FCSTD DOCUMENT  (FreeCAD 0.22R37730 (Git))
Label: Прокладка
License: All rights reserved
LicenseURL: https://en.wikipedia.org/wiki/All_rights_reserved
objects: Image::ImagePlane×1, Sketcher::SketchObject×1, PartDesign::Body×1
note: 2 computed .brp shape members not serialized (recipe doc carries the construction recipe); baked Part::Feature solids carry a one-line shape summary decoded from their .brp

FEATURE [Image::ImagePlane] Scan
  Placement = pos=(31.0997,3.57913,0) rot=(0,0,-1;1.91986rad)
  XSize = 66.6751
  YSize = 122.428
FEATURE [Sketcher::SketchObject] Sketch
  AttachmentSupport = -> [XY_Plane]
  FullyConstrained = true
  MapMode = 5
  Support = -> [XY_Plane]
  expr: Constraints[15] = 43 - 6.5
  expr: Constraints[18] = 57 - 6.5
  expr: Constraints[27] = 43.5 - 21.5 / 2 - 6.5 / 2
  expr: Constraints[39] = 103.5 - 6.5 / 2 - 16 / 2
  expr: Constraints[40] = 33.5 - 21.5 / 2 - 6.5 / 2
  expr: Constraints[41] = 68 - 6.5
  expr: Constraints[42] = 90.5 - 6.5 / 2 - 16 / 2
  expr: Constraints[6] = 72 - 6.5
  expr: Constraints[9] = 26.5 - 6.5
  sketch-geometry (26):
    g0: Circle CenterX=0 CenterY=0 CenterZ=0 NormalX=0 NormalY=0 NormalZ=1 AngleXU=0 Radius=3.25
    g1: Circle CenterX=20 CenterY=5.23129 CenterZ=0 NormalX=0 NormalY=0 NormalZ=1 AngleXU=0 Radius=3.25
    g2: Circle CenterX=81.5 CenterY=5.23129 CenterZ=0 NormalX=0 NormalY=0 NormalZ=1 AngleXU=0 Radius=3.25
    g3: Circle CenterX=60.6524 CenterY=-24.7292 CenterZ=0 NormalX=0 NormalY=0 NormalZ=1 AngleXU=0 Radius=3.25
    g4: LineSegment StartX=0 StartY=0 StartZ=0 EndX=60.6524 EndY=-24.7292 EndZ=0
    g5: LineSegment StartX=0 StartY=0 StartZ=0 EndX=20 EndY=5.23129 EndZ=0
    g6: LineSegment StartX=20 StartY=5.23129 StartZ=0 EndX=81.5 EndY=5.23129 EndZ=0
    g7: LineSegment StartX=60.6524 StartY=-24.7292 StartZ=0 EndX=81.5 EndY=5.23129 EndZ=0
    g8: LineSegment StartX=20 StartY=5.23129 StartZ=0 EndX=60.6524 EndY=-24.7292 EndZ=0
    g9: LineSegment StartX=0 StartY=0 StartZ=0 EndX=81.5 EndY=5.23129 EndZ=0
    g10: Circle CenterX=54.3385 CenterY=-6.27967 CenterZ=0 NormalX=0 NormalY=0 NormalZ=1 AngleXU=0 Radius=10.75
    g11: LineSegment StartX=54.3385 StartY=-6.27967 StartZ=0 EndX=60.6524 EndY=-24.7292 EndZ=0
    g12: LineSegment StartX=54.3385 StartY=-6.27967 StartZ=0 EndX=81.5 EndY=5.23129 EndZ=0
    g13: Circle CenterX=54.3385 CenterY=-6.27967 CenterZ=0 NormalX=0 NormalY=0 NormalZ=1 AngleXU=0 Radius=14.25
    g14: Circle CenterX=-10.6318 CenterY=9.89908 CenterZ=0 NormalX=0 NormalY=0 NormalZ=1 AngleXU=0 Radius=8
    g15: LineSegment StartX=-10.6318 StartY=9.89908 StartZ=0 EndX=60.6524 EndY=-24.7292 EndZ=0
    g16: LineSegment StartX=-10.6318 StartY=9.89908 StartZ=0 EndX=54.3385 EndY=-6.27967 EndZ=0
    g17: LineSegment StartX=-10.6318 StartY=9.89908 StartZ=0 EndX=81.5 EndY=5.23129 EndZ=0
    g18: LineSegment StartX=-10.6318 StartY=9.89908 StartZ=0 EndX=0 EndY=0 EndZ=0
    g19: Circle CenterX=0 CenterY=0 CenterZ=0 NormalX=0 NormalY=0 NormalZ=1 AngleXU=0 Radius=3.25
    g20: Circle CenterX=20 CenterY=5.23129 CenterZ=0 NormalX=0 NormalY=0 NormalZ=1 AngleXU=0 Radius=3.25
    g21: Circle CenterX=81.5 CenterY=5.23129 CenterZ=0 NormalX=0 NormalY=0 NormalZ=1 AngleXU=0 Radius=3.25
    g22: Circle CenterX=60.6524 CenterY=-24.7292 CenterZ=0 NormalX=0 NormalY=0 NormalZ=1 AngleXU=0 Radius=3.25
    g23: Circle CenterX=60.6524 CenterY=-24.7292 CenterZ=0 NormalX=0 NormalY=0 NormalZ=1 AngleXU=0 Radius=6.25
    g24: Circle CenterX=0 CenterY=0 CenterZ=0 NormalX=0 NormalY=0 NormalZ=1 AngleXU=0 Radius=7.25
    g25: LineSegment StartX=58.3971 StartY=3.67474 StartZ=0 EndX=47.0708 EndY=-24.105 EndZ=0
  constraints (59):
    c: Diameter(g0) = 6.5
    c: Diameter(g1) = 6.5
    c: Diameter(g2) = 6.5
    c: Diameter(g3) = 6.5
    c: Coincident(g4,g0)
    c: Coincident(g4,g3)
    c: Distance(g4,g4) = 65.5
    c: Coincident(g5,g0)
    c: Coincident(g5,g1)
    c: DistanceX(g5,g5) = 20
    c: Coincident(g6,g1)
    c: Coincident(g6,g2)
    c: Horizontal(g6)
    c: Coincident(g7,g3)
    c: Coincident(g7,g2)
    c: Distance(g7,g7) = 36.5
    c: Coincident(g8,g1)
    c: Coincident(g8,g3)
    c: Distance(g8,g8) = 50.5
    c: Coincident(g0,g9)
    c: Coincident(g2,g9)
    c: Coincident(g0,g-1)
    c: Diameter(g10) = 21.5
    c: Coincident(g11,g10)
    c: Coincident(g11,g3)
    c: Coincident(g12,g10)
    c: Coincident(g12,g2)
    c: Distance(g12,g12) = 29.5
    c: Coincident(g10,g13)
    c: Distance(g10,g13) = 3.5
    c: Diameter(g14) = 16
    c: Coincident(g15,g14)
    c: Coincident(g15,g3)
    c: Coincident(g16,g14)
    c: Coincident(g16,g10)
    c: Coincident(g17,g14)
    c: Coincident(g17,g2)
    c: Coincident(g18,g14)
    c: Coincident(g18,g0)
    c: Distance(g17,g17) = 92.25
    c: Distance(g11,g11) = 19.5
    c: Distance(g6) = 61.5
    c: Distance(g15) = 79.25
    c: Coincident(g19,g0)
    c: Equal(g19,g0)
    c: Coincident(g20,g1)
    c: Equal(g1,g20)
    c: Coincident(g21,g2)
    c: Equal(g21,g2)
    c: Coincident(g22,g3)
    c: Equal(g22,g3)
    c: Coincident(g23,g3)
    c: Distance(g23,g22) = 3
    c: Coincident(g24,g0)
    c: Distance(g24,g19) = 4
    c: PointOnObject(g25,g10)
    c: Distance(g25,g25) = 30
    c: PointOnObject(g10,g25)
    c: Perpendicular(g4,g25)
FEATURE [PartDesign::Body] Body  label="Тело"
  AllowCompound = false
  Group = -> [Sketch]
  Origin = -> Origin
